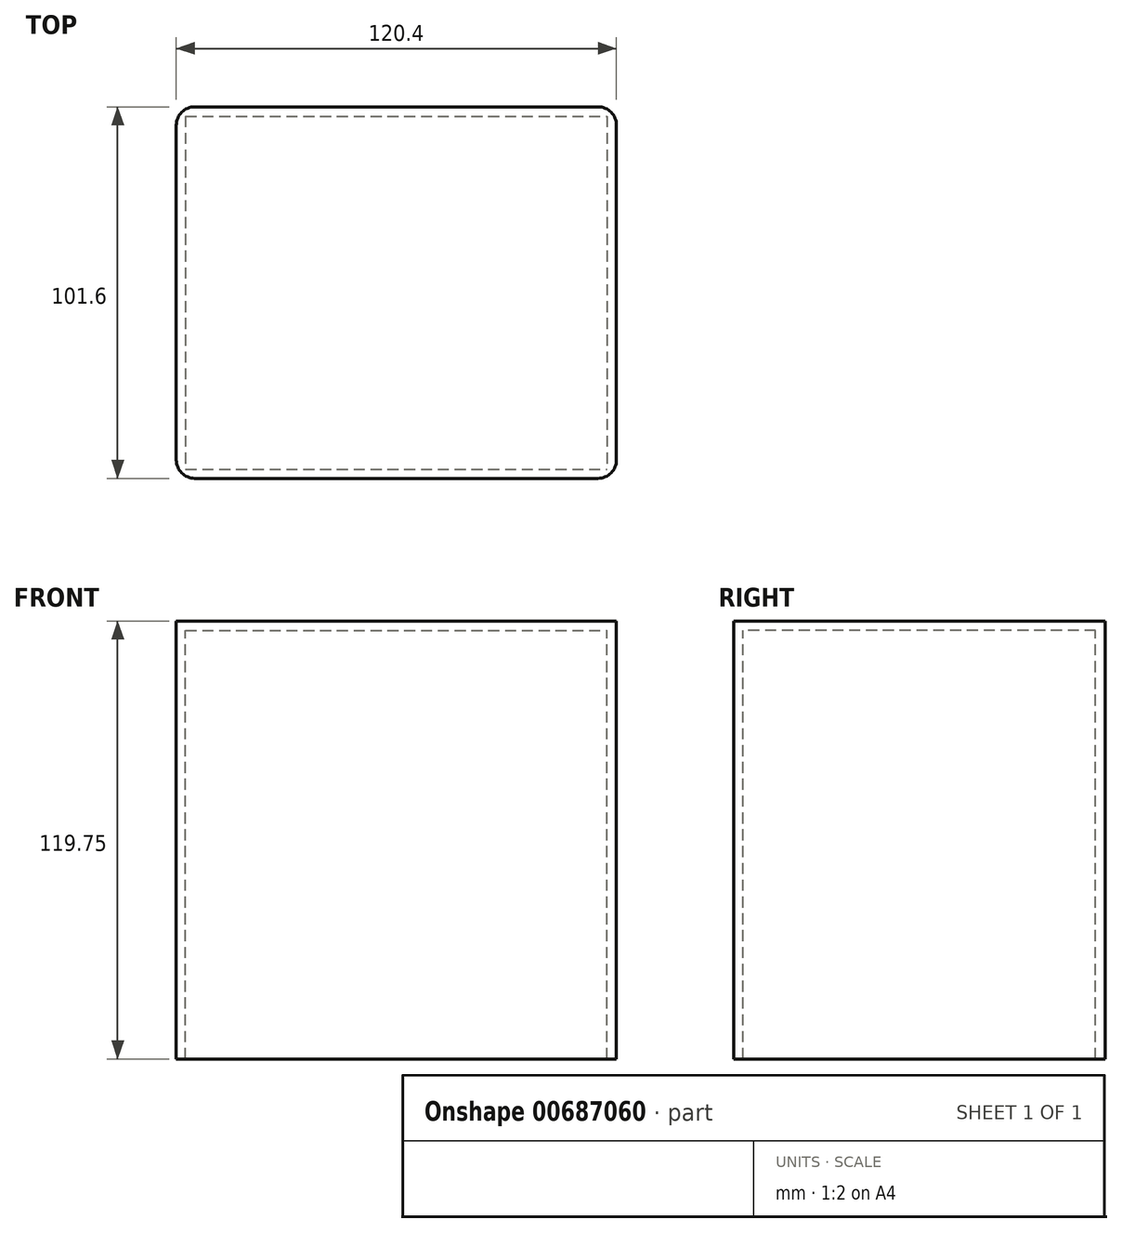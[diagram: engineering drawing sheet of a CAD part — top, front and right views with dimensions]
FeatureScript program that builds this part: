
annotation { "Feature Type Name" : "Feature", "Feature Type Description" : "" }
export const myFeature = defineFeature(function(context is Context, id is Id, definition is map)
    precondition{}
    {
        {
            var Q0;
            Q0=qCreatedBy(makeId("Top.planeOp"),FACE);
            var sketch = newSketch(context, id + "F0", { "sketchPlane" : qUnion([Q0])});
            skLineSegment(sketch, "E0.bottom", {"start": v(-58.97, 48.37) * mm, "end": v(61.43, 48.37) * mm});
            skLineSegment(sketch, "E0.top", {"start": v(-58.97, -53.23) * mm, "end": v(61.43, -53.23) * mm});
            skLineSegment(sketch, "E0.left", {"start": v(-58.97, 48.37) * mm, "end": v(-58.97, -53.23) * mm});
            skLineSegment(sketch, "E0.right", {"start": v(61.43, 48.37) * mm, "end": v(61.43, -53.23) * mm});
            skSolve(sketch);
        }
        {
            var Q0;
            Q0=makeQuery(id+"F0.imprint","IMPRINT",FACE,{"disambiguationData":[TD([[makeQuery(id+"F0.imprint","IMPRINT",EDGE,{"derivedFrom":sQuery(id+"F0.wireOp",EDGE,"E0.bottom")}),-1.0]])]});
            extrude(context, id + "F1", {"entities" : qUnion([Q0]), "oppositeDirection" : true, "depth" : 119.75 * mm, "offsetDistance" : 25.4 * mm});
        }
        {
            var Q0;
            Q0=makeQuery(id+"F1.opExtrude","CAP_FACE",FACE,{"disambiguationData":[OSD([sQuery(id+"F0.wireOp",EDGE,"E0.bottom"),sQuery(id+"F0.wireOp",EDGE,"E0.top"),sQuery(id+"F0.wireOp",EDGE,"E0.left"),sQuery(id+"F0.wireOp",EDGE,"E0.right")])],"isStart":false});
            shell(context, id + "F2", {"entities" : qUnion([Q0]), "thickness" : 2.54 * mm});
        }
        {
            var Q0;
            Q0=makeQuery(id+"F1.opExtrude","SWEPT_EDGE",EDGE,{"disambiguationData":[OSD([sQuery(id+"F0.wireOp",EDGE,"E0.bottom"),sQuery(id+"F0.wireOp",EDGE,"E0.right")])]});
            var Q1;
            Q1=makeQuery(id+"F1.opExtrude","SWEPT_EDGE",EDGE,{"disambiguationData":[OSD([sQuery(id+"F0.wireOp",EDGE,"E0.bottom"),sQuery(id+"F0.wireOp",EDGE,"E0.left")])]});
            var Q2;
            Q2=makeQuery(id+"F1.opExtrude","SWEPT_EDGE",EDGE,{"disambiguationData":[OSD([sQuery(id+"F0.wireOp",EDGE,"E0.top"),sQuery(id+"F0.wireOp",EDGE,"E0.left")])]});
            var Q3;
            Q3=makeQuery(id+"F1.opExtrude","SWEPT_EDGE",EDGE,{"disambiguationData":[OSD([sQuery(id+"F0.wireOp",EDGE,"E0.top"),sQuery(id+"F0.wireOp",EDGE,"E0.right")])]});
            fillet(context, id + "F3", {"entities" : qUnion([Q0, Q1, Q2, Q3]), "radius" : 5.08 * mm, "tangentPropagation" : true, "allowEdgeOverflow" : false});
        }
    });
